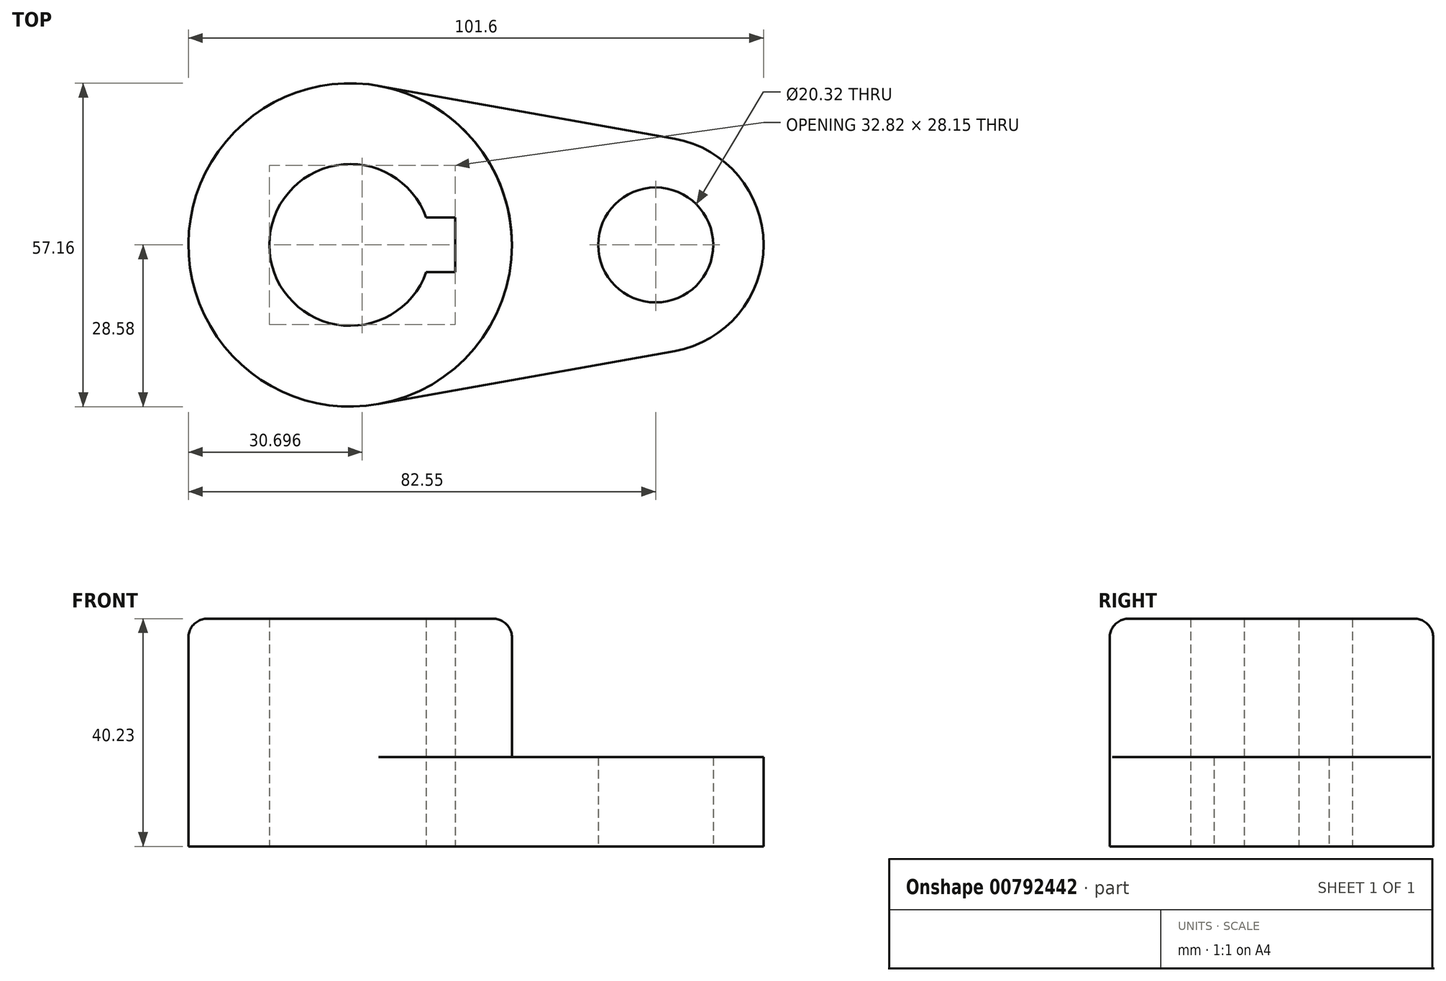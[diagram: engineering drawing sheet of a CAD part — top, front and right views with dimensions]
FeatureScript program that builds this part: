
annotation { "Feature Type Name" : "Feature", "Feature Type Description" : "" }
export const myFeature = defineFeature(function(context is Context, id is Id, definition is map)
    precondition{}
    {
        {
            var Q0;
            Q0=qCreatedBy(makeId("Top.planeOp"),FACE);
            var sketch = newSketch(context, id + "F0", { "sketchPlane" : qUnion([Q0])});
            skCircle(sketch, "E0", {"center": v(-35.94, 0) * mm, "radius": 14.29 * mm});
            skCircle(sketch, "E1", {"center": v(-35.94, 0) * mm, "radius": 28.58 * mm});
            skCircle(sketch, "E2", {"center": v(18.03, 0) * mm, "radius": 10.16 * mm});
            skArc(sketch, "E3", {"start": v(21.4, -18.75) * mm, "mid": v(37.08, 0) * mm, "end": v(21.4, 18.75) * mm});
            skLineSegment(sketch, "E4", {"start": v(-30.9, 28.13) * mm, "end": v(21.4, 18.75) * mm});
            skLineSegment(sketch, "E5", {"start": v(-30.9, -28.13) * mm, "end": v(21.4, -18.75) * mm});
            skLineSegment(sketch, "E6.bottom", {"start": v(-49.4, -4.83) * mm, "end": v(-17.42, -4.83) * mm});
            skLineSegment(sketch, "E6.top", {"start": v(-49.4, 4.83) * mm, "end": v(-17.42, 4.83) * mm});
            skLineSegment(sketch, "E6.right", {"start": v(-17.42, -4.83) * mm, "end": v(-17.42, 4.83) * mm});
            skPoint(sketch, "E7.orphan", {"position": v(-54.47, 4.83) * mm});
            skPoint(sketch, "E8.orphan", {"position": v(-54.47, -4.83) * mm});
            skSolve(sketch);
        }
        {
            var Q0;
            {var subQ7=sQuery(id+"F0.wireOp",EDGE,"E6.right");Q0=makeQuery(id+"F0.imprint","IMPRINT",FACE,{"disambiguationData":[TD([[makeQuery(id+"F0.imprint","IMPRINT",EDGE,{"derivedFrom":subQ7}),-1.0]])]});}
            extrude(context, id + "F1", {"entities" : qUnion([Q0]), "depth" : 40.23 * mm, "offsetDistance" : 25.4 * mm});
        }
        {
            var Q0;
            Q0=makeQuery(id+"F0.imprint","IMPRINT",FACE,{"disambiguationData":[TD([[makeQuery(id+"F0.imprint","IMPRINT",EDGE,{"derivedFrom":sQuery(id+"F0.wireOp",EDGE,"E2")}),-1.0]])]});
            extrude(context, id + "F2", {"entities" : qUnion([Q0]), "operationType" : NewBodyOperationType.ADD, "depth" : 15.77 * mm, "offsetDistance" : 25.4 * mm});
        }
        {
            var Q0;
            Q0=makeQuery(id+"F1.opExtrude","CAP_EDGE",EDGE,{"disambiguationData":[OSD([sQuery(id+"F0.wireOp",EDGE,"E1")])],"isStart":false});
            fillet(context, id + "F3", {"entities" : qUnion([Q0]), "radius" : 3.3 * mm, "tangentPropagation" : true, "allowEdgeOverflow" : false});
        }
    });
